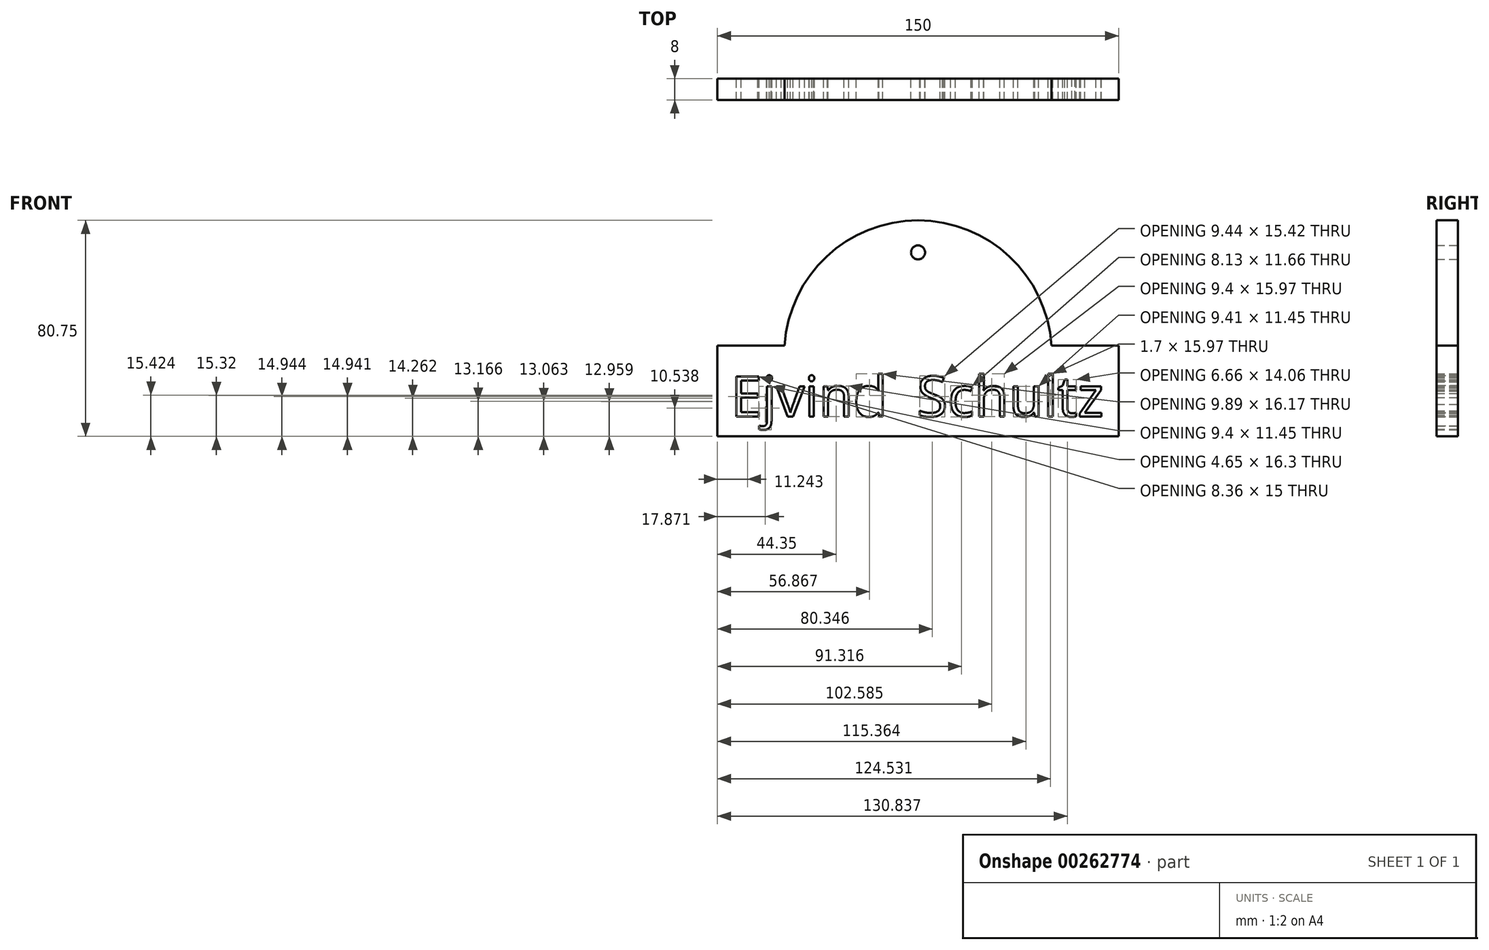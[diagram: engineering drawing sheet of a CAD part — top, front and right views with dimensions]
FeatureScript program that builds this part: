
annotation { "Feature Type Name" : "Feature", "Feature Type Description" : "" }
export const myFeature = defineFeature(function(context is Context, id is Id, definition is map)
    precondition{}
    {
        {
            var Q0;
            Q0=qCreatedBy(makeId("Front.planeOp"),FACE);
            var sketch = newSketch(context, id + "F0", { "sketchPlane" : qUnion([Q0])});
            skLineSegment(sketch, "E0.bottom", {"start": v(-75, 14.34) * mm, "end": v(75, 14.34) * mm});
            skLineSegment(sketch, "E0.top", {"start": v(-75, -19.65) * mm, "end": v(75, -19.65) * mm});
            skLineSegment(sketch, "E0.left", {"start": v(-75, 14.34) * mm, "end": v(-75, -19.65) * mm});
            skLineSegment(sketch, "E0.right", {"start": v(75, 14.34) * mm, "end": v(75, -19.65) * mm});
            skArc(sketch, "E1", {"start": v(49.9, 14.34) * mm, "mid": v(0, 61.1) * mm, "end": v(-49.9, 14.34) * mm});
            skCircle(sketch, "E2", {"center": v(0, 49.14) * mm, "radius": 2.61 * mm});
            skText(sketch, "E3", { "text": "Ejvind  Schultz", "fontName": "OpenSans-Regular.ttf"});
            skPoint(sketch, "E4", {"position": v(0, 14.34) * mm});
            const initialGuessF0  = {"E3": [-0.07, -0.01221, 1, 0, 0.01513]};
            skSetInitialGuess(sketch, initialGuessF0);
            skSolve(sketch);
        }
        {
            var Q0;
            Q0 = qSketchRegion(id + "F0", true);
            extrude(context, id + "F1", {"entities" : qUnion([Q0]), "depth" : 8 * mm});
        }
    });
